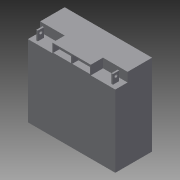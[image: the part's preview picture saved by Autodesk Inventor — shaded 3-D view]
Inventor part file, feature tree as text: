
AUTODESK INVENTOR PART (.ipt)
format: ipt  version: 2015 SP1 (Build 190203100, 203)  size: 185,856 bytes
history: native  units: in
note: dims shown in document units (in); Inventor stores cm internally (conversion verified against a paired STEP export)
features: extrude x7, sketch x7, projected_geometry x7
ambient origin geometry x8: Origin, YZ Plane, XZ Plane, XY Plane, X Axis, Y Axis, Z Axis, Center Point
bodies: Solid1 (feature_tree)
feature tree (21):
  extrude  "Extrusion1"  Depth=3.0in
  extrude  "Extrusion2"  Depth=2.0in
  extrude  "Extrusion3"  Depth=2.0in
  extrude  "Extrusion4"  Depth=0.75in TaperAngle=0.0deg
  extrude  "Extrusion5"  Depth=1.45in
  extrude  "Extrusion6"  Depth=0.5in TaperAngle=0.0deg
  extrude  "Extrusion7"  Depth=1.69in
  sketch  "Sketch1"  dims[d0=7.125in d1=3.0in]
  sketch  "Sketch2"  dims[d2=6.625in d3=0.0in d4=2.0in]
  projected_geometry  "Projected Loop1"
  sketch  "Sketch3"  dims[d5=1.0in d6=2.0in]
  projected_geometry  "Projected Loop2"
  sketch  "Sketch4"  dims[d7=1.0in d8=0.75in d9=0.0in]
  projected_geometry  "Projected Loop3"
  sketch  "Sketch5"  dims[d10=0.0625in d11=1.45in]
  projected_geometry  "Projected Loop4"
  projected_geometry  "Projected Loop5"
  sketch  "Sketch6"  dims[d12=1.45in d13=0.5in d14=0.0in]
  projected_geometry  "Projected Loop6"
  sketch  "Sketch7"  dims[d15=0.0625in d16=1.69in d17=1.69in d18=1.69in d19=1.69in d20=0.0625in d21=0.0625in d22=0.5in d23=0.0in d24=0.5in d25=0.5in d26=0.5in d27=0.5in d28=0.125in d29=0.5in d30=0.125in d31=0.5in d32=0.75in d33=0.0in d34=0.25in d35=0.25in d36=0.25in d37=1.0in d38=0.0in d39=0.25in d40=0.25in d41=0.25in d42=1.0in d43=0.0in]
  projected_geometry  "Projected Loop7"
